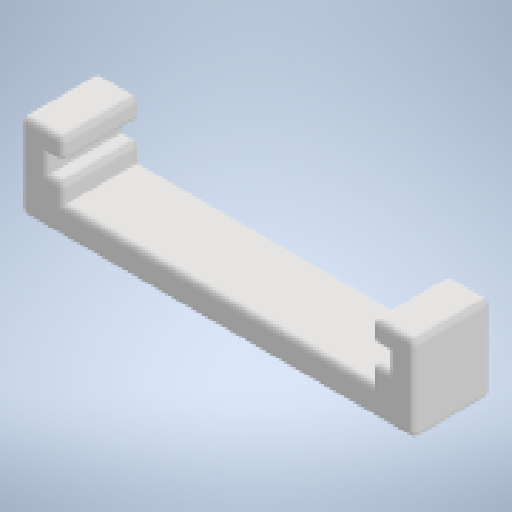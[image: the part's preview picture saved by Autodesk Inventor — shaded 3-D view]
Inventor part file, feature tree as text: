
AUTODESK INVENTOR PART (.ipt)
format: ipt  version: 2024.2 (Build 282272000, 272)  size: 242,176 bytes
history: native  units: mm
features: other x1, extrude x1, fillet x1, sketch x1
ambient origin geometry x8: Origin, YZ Plane, XZ Plane, XY Plane, X Axis, Y Axis, Z Axis, Center Point
bodies: Body1 (feature_tree)
feature tree (4):
  other  "Bryła1"
  extrude  "Wyciągnięcie proste1"  Depth=107.0mm
  fillet  "Zaokrąglenie1"  Radius=5.0mm
  sketch  "Szkic1"
